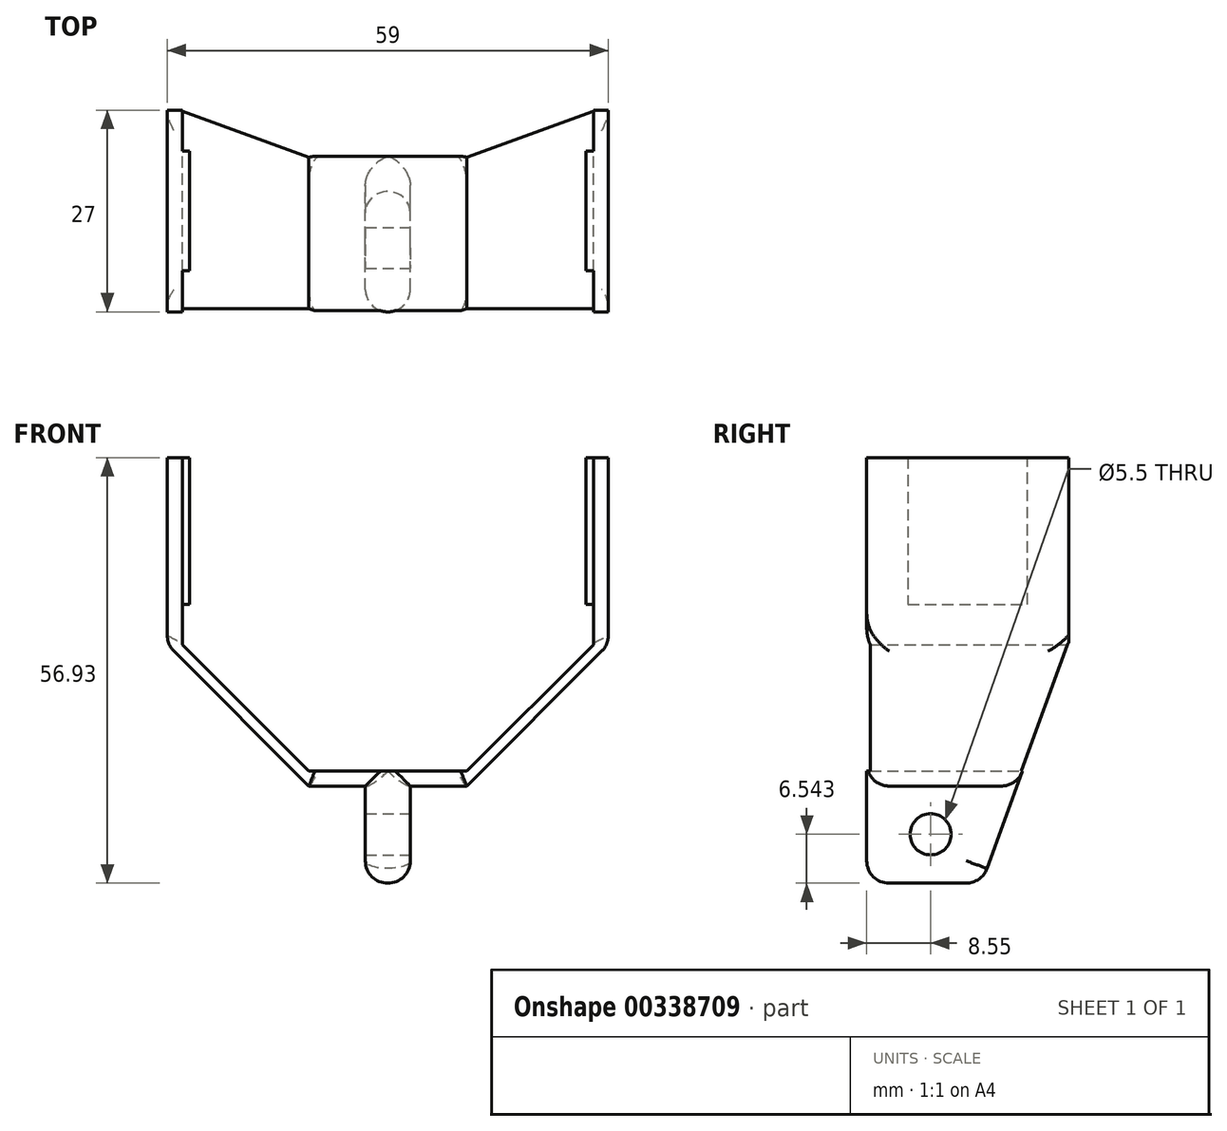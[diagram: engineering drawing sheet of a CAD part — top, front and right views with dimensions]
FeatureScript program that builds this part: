
annotation { "Feature Type Name" : "Feature", "Feature Type Description" : "" }
export const myFeature = defineFeature(function(context is Context, id is Id, definition is map)
    precondition{}
    {
        {
            var Q0;
            Q0=qCreatedBy(makeId("Front.planeOp"),FACE);
            var sketch = newSketch(context, id + "F0", { "sketchPlane" : qUnion([Q0])});
            skLineSegment(sketch, "E0", {"start": v(-27.5, 0) * mm, "end": v(-27.5, 25) * mm});
            skLineSegment(sketch, "E1", {"start": v(-27.5, 25) * mm, "end": v(-29.5, 25) * mm});
            skLineSegment(sketch, "E2", {"start": v(-29.5, 25) * mm, "end": v(-29.5, 0) * mm});
            skLineSegment(sketch, "E3", {"start": v(-29.5, 0) * mm, "end": v(-10.57, -18.93) * mm});
            skLineSegment(sketch, "E4", {"start": v(-27.5, 0) * mm, "end": v(-10.57, -16.93) * mm});
            skLineSegment(sketch, "E5", {"start": v(0, -16.93) * mm, "end": v(-10.57, -16.93) * mm});
            skLineSegment(sketch, "E6", {"start": v(0, -18.93) * mm, "end": v(-10.57, -18.93) * mm});
            skPoint(sketch, "E7.orphan", {"position": v(0, -27.5) * mm});
            skPoint(sketch, "E8.orphan", {"position": v(0, -29.5) * mm});
            skLineSegment(sketch, "E9", {"start": v(-27.5, 0) * mm, "end": v(-27.5, 3.34) * mm});
            skLineSegment(sketch, "E10", {"start": v(-3, -18.93) * mm, "end": v(-3, -31.93) * mm});
            skLineSegment(sketch, "E11", {"start": v(-3, -31.93) * mm, "end": v(0, -31.93) * mm});
            skLineSegment(sketch, "E12", {"start": v(0, -31.93) * mm, "end": v(0, -16.93) * mm});
            skSolve(sketch);
        }
        {
            var Q0;
            {var subQ3=sQuery(id+"F0.wireOp",EDGE,"E10");Q0=makeQuery(id+"F0.imprint","IMPRINT",FACE,{"disambiguationData":[TD([[makeQuery(id+"F0.imprint","IMPRINT",EDGE,{"derivedFrom":subQ3}),1.0]])]});}
            var Q1;
            {var subQ2=sQuery(id+"F0.wireOp",EDGE,"27ad3184-4ef8-43b1-b54a-c4742ede5e2c0.MirrorCS");Q1=makeQuery(id+"F0.imprint","IMPRINT",FACE,{"disambiguationData":[TD([[makeQuery(id+"F0.imprint","IMPRINT",EDGE,{"derivedFrom":subQ2}),-1.0]])]});}
            var Q2;
            {var subQ0=sQuery(id+"F0.wireOp",EDGE,"27ad3184-4ef8-43b1-b54a-c4742ede5e2c1.MirrorCS");Q2=makeQuery(id+"F0.imprint","IMPRINT",FACE,{"disambiguationData":[TD([[makeQuery(id+"F0.imprint","IMPRINT",EDGE,{"derivedFrom":subQ0}),-1.0]])]});}
            var Q3;
            Q3=makeQuery(id+"F0.imprint","IMPRINT",FACE,{"disambiguationData":[TD([[makeQuery(id+"F0.imprint","IMPRINT",EDGE,{"derivedFrom":sQuery(id+"F0.wireOp",EDGE,"E0")}),1.0]])]});
            extrude(context, id + "F1", {"entities" : qUnion([Q0, Q1, Q2, Q3]), "endBound" : BoundingType.SYMMETRIC, "depth" : 27 * mm});
        }
        {
            var Q0;
            Q0=makeQuery(id+"F1.opExtrude","SWEPT_FACE",FACE,{"disambiguationData":[OSD([sQuery(id+"F0.wireOp",EDGE,"E0"),sQuery(id+"F0.wireOp",EDGE,"E9")])]});
            var sketch = newSketch(context, id + "F2", { "sketchPlane" : qUnion([Q0])});
            skLineSegment(sketch, "E13", {"start": v(-8, 25) * mm, "end": v(-8, 5.4) * mm});
            skLineSegment(sketch, "E14", {"start": v(-8, 5.4) * mm, "end": v(8, 5.4) * mm});
            skLineSegment(sketch, "E15", {"start": v(8, 5.4) * mm, "end": v(8, 25) * mm});
            skLineSegment(sketch, "E16", {"start": v(8, 25) * mm, "end": v(-8, 25) * mm});
            skSolve(sketch);
        }
        {
            var Q0;
            Q0=makeQuery(id+"F2.imprint","IMPRINT",FACE,{"disambiguationData":[TD([[makeQuery(id+"F2.imprint","IMPRINT",EDGE,{"derivedFrom":sQuery(id+"F2.wireOp",EDGE,"E13")}),1.0]])]});
            extrude(context, id + "F3", {"entities" : qUnion([Q0]), "operationType" : NewBodyOperationType.ADD, "depth" : 1 * mm});
        }
        {
            var Q0;
            Q0=makeQuery(id+"F1.opExtrude","SWEPT_BODY",BODY,{"disambiguationData":[OSD([sQuery(id+"F0.wireOp",EDGE,"E0"),sQuery(id+"F0.wireOp",EDGE,"E1"),sQuery(id+"F0.wireOp",EDGE,"E2"),sQuery(id+"F0.wireOp",EDGE,"E3"),sQuery(id+"F0.wireOp",EDGE,"E4"),sQuery(id+"F0.wireOp",EDGE,"E5"),sQuery(id+"F0.wireOp",EDGE,"E6"),sQuery(id+"F0.wireOp",EDGE,"E9"),sQuery(id+"F0.wireOp",EDGE,"E10"),sQuery(id+"F0.wireOp",EDGE,"E11"),sQuery(id+"F0.wireOp",EDGE,"E12")])]});
            var Q1;
            Q1=qCreatedBy(makeId("Right.planeOp"),FACE);
            mirror(context, id + "F4", {"operationType" : NewBodyOperationType.ADD, "entities" : qUnion([Q0]), "mirrorPlane" : qUnion([Q1])});
        }
        {
            var Q0;
            Q0=makeQuery(id+"F1.opExtrude","SWEPT_FACE",FACE,{"disambiguationData":[OSD([sQuery(id+"F0.wireOp",EDGE,"E2")])]});
            var sketch = newSketch(context, id + "F5", { "sketchPlane" : qUnion([Q0])});
            skLineSegment(sketch, "E17.MirrorCS", {"start": v(-21.23, 0) * mm, "end": v(-13.5, 0) * mm});
            skLineSegment(sketch, "E18.MirrorCS", {"start": v(-13.5, 0) * mm, "end": v(0.18, -37.59) * mm});
            skLineSegment(sketch, "E19.MirrorCS", {"start": v(-6.55, -39.4) * mm, "end": v(-25.06, -39.4) * mm});
            skLineSegment(sketch, "E20.MirrorCS", {"start": v(-25.06, -39.4) * mm, "end": v(-21.23, 0) * mm});
            skLineSegment(sketch, "E21", {"start": v(-6.55, -39.4) * mm, "end": v(0.18, -37.59) * mm});
            skSolve(sketch);
        }
        {
            var Q0;
            Q0 = qSketchRegion(id + "F5", true);
            extrude(context, id + "F6", {"entities" : qUnion([Q0]), "operationType" : NewBodyOperationType.REMOVE, "endBound" : BoundingType.SYMMETRIC, "depth" : 10000 * mm});
        }
        {
            var Q0;
            Q0=makeQuery(id+"F4.opPattern","COPY",FACE,{"derivedFrom":makeQuery(id+"F1.opExtrude","SWEPT_FACE",FACE,{"disambiguationData":[OSD([sQuery(id+"F0.wireOp",EDGE,"E10")])]}),"instanceName":"1"});
            var sketch = newSketch(context, id + "F7", { "sketchPlane" : qUnion([Q0])});
            skCircle(sketch, "E22", {"center": v(-4.95, -25.39) * mm, "radius": 2.75 * mm});
            skSolve(sketch);
        }
        {
            var Q0;
            Q0=makeQuery(id+"F7.imprint","IMPRINT",FACE,{"disambiguationData":[TD([[makeQuery(id+"F7.imprint","IMPRINT",EDGE,{"derivedFrom":sQuery(id+"F7.wireOp",EDGE,"E22")}),1.0]])]});
            extrude(context, id + "F8", {"entities" : qUnion([Q0]), "operationType" : NewBodyOperationType.REMOVE, "endBound" : BoundingType.SYMMETRIC, "oppositeDirection" : true, "depth" : 100 * mm});
        }
        {
            var Q0;
            {var subQ0=makeQuery(id+"F1.opExtrude","SWEPT_FACE",FACE,{"disambiguationData":[OSD([sQuery(id+"F0.wireOp",EDGE,"E11")])]});Q0=makeQuery(id+"F4.boolean.opBoolean","MERGE",FACE,{"derivedFrom":[subQ0,makeQuery(id+"F4.opPattern","COPY",FACE,{"derivedFrom":subQ0,"instanceName":"1"})]});}
            fillet(context, id + "F9", {"entities" : qUnion([Q0]), "radius" : 3 * mm, "tangentPropagation" : true, "allowEdgeOverflow" : false});
        }
        {
            var Q0;
            Q0=makeQuery(id+"F4.opPattern","COPY",EDGE,{"derivedFrom":makeQuery(id+"F1.opExtrude","CAP_EDGE",EDGE,{"disambiguationData":[OSD([sQuery(id+"F0.wireOp",EDGE,"E10")])],"isStart":false}),"instanceName":"1"});
            var Q1;
            Q1=makeQuery(id+"F1.opExtrude","CAP_EDGE",EDGE,{"disambiguationData":[OSD([sQuery(id+"F0.wireOp",EDGE,"E10")])],"isStart":false});
            var Q2;
            Q2=makeQuery(id+"F4.opPattern","COPY",EDGE,{"derivedFrom":makeQuery(id+"F1.opExtrude","CAP_EDGE",EDGE,{"disambiguationData":[OSD([sQuery(id+"F0.wireOp",EDGE,"E6")])],"isStart":false}),"instanceName":"1"});
            var Q3;
            Q3=makeQuery(id+"F1.opExtrude","CAP_EDGE",EDGE,{"disambiguationData":[OSD([sQuery(id+"F0.wireOp",EDGE,"E6")])],"isStart":false});
            var Q4;
            Q4=makeQuery(id+"F1.opExtrude","CAP_EDGE",EDGE,{"disambiguationData":[OSD([sQuery(id+"F0.wireOp",EDGE,"E3")])],"isStart":false});
            var Q5;
            Q5=makeQuery(id+"F4.opPattern","COPY",EDGE,{"derivedFrom":makeQuery(id+"F1.opExtrude","CAP_EDGE",EDGE,{"disambiguationData":[OSD([sQuery(id+"F0.wireOp",EDGE,"E3")])],"isStart":false}),"instanceName":"1"});
            var Q6;
            Q6=makeQuery(id+"F6.boolean.opBoolean","INTERSECT",EDGE,{"derivedFrom":[makeQuery(id+"F4.opPattern","COPY",FACE,{"derivedFrom":makeQuery(id+"F1.opExtrude","SWEPT_FACE",FACE,{"disambiguationData":[OSD([sQuery(id+"F0.wireOp",EDGE,"E3")])]}),"instanceName":"1"}),makeQuery(id+"F6.opExtrude","SWEPT_FACE",FACE,{"disambiguationData":[OSD([sQuery(id+"F5.wireOp",EDGE,"E18.MirrorCS")])]})]});
            var Q7;
            Q7=makeQuery(id+"F6.boolean.opBoolean","INTERSECT",EDGE,{"derivedFrom":[makeQuery(id+"F4.opPattern","COPY",FACE,{"derivedFrom":makeQuery(id+"F1.opExtrude","SWEPT_FACE",FACE,{"disambiguationData":[OSD([sQuery(id+"F0.wireOp",EDGE,"E6")])]}),"instanceName":"1"}),makeQuery(id+"F6.opExtrude","SWEPT_FACE",FACE,{"disambiguationData":[OSD([sQuery(id+"F5.wireOp",EDGE,"E18.MirrorCS")])]})]});
            var Q8;
            Q8=makeQuery(id+"F6.boolean.opBoolean","INTERSECT",EDGE,{"derivedFrom":[makeQuery(id+"F4.opPattern","COPY",FACE,{"derivedFrom":makeQuery(id+"F1.opExtrude","SWEPT_FACE",FACE,{"disambiguationData":[OSD([sQuery(id+"F0.wireOp",EDGE,"E10")])]}),"instanceName":"1"}),makeQuery(id+"F6.opExtrude","SWEPT_FACE",FACE,{"disambiguationData":[OSD([sQuery(id+"F5.wireOp",EDGE,"E18.MirrorCS")])]})]});
            var Q9;
            Q9=makeQuery(id+"F6.boolean.opBoolean","INTERSECT",EDGE,{"derivedFrom":[makeQuery(id+"F1.opExtrude","SWEPT_FACE",FACE,{"disambiguationData":[OSD([sQuery(id+"F0.wireOp",EDGE,"E10")])]}),makeQuery(id+"F6.opExtrude","SWEPT_FACE",FACE,{"disambiguationData":[OSD([sQuery(id+"F5.wireOp",EDGE,"E18.MirrorCS")])]})]});
            var Q10;
            Q10=makeQuery(id+"F6.boolean.opBoolean","INTERSECT",EDGE,{"derivedFrom":[makeQuery(id+"F1.opExtrude","SWEPT_FACE",FACE,{"disambiguationData":[OSD([sQuery(id+"F0.wireOp",EDGE,"E6")])]}),makeQuery(id+"F6.opExtrude","SWEPT_FACE",FACE,{"disambiguationData":[OSD([sQuery(id+"F5.wireOp",EDGE,"E18.MirrorCS")])]})]});
            var Q11;
            Q11=makeQuery(id+"F6.boolean.opBoolean","INTERSECT",EDGE,{"derivedFrom":[makeQuery(id+"F1.opExtrude","SWEPT_FACE",FACE,{"disambiguationData":[OSD([sQuery(id+"F0.wireOp",EDGE,"E3")])]}),makeQuery(id+"F6.opExtrude","SWEPT_FACE",FACE,{"disambiguationData":[OSD([sQuery(id+"F5.wireOp",EDGE,"E18.MirrorCS")])]})]});
            var Q12;
            Q12=makeQuery(id+"F4.opPattern","COPY",EDGE,{"derivedFrom":makeQuery(id+"F1.opExtrude","SWEPT_EDGE",EDGE,{"disambiguationData":[OSD([sQuery(id+"F0.wireOp",EDGE,"E2"),sQuery(id+"F0.wireOp",EDGE,"E3")])]}),"instanceName":"1"});
            var Q13;
            Q13=makeQuery(id+"F1.opExtrude","SWEPT_EDGE",EDGE,{"disambiguationData":[OSD([sQuery(id+"F0.wireOp",EDGE,"E2"),sQuery(id+"F0.wireOp",EDGE,"E3")])]});
            fillet(context, id + "F10", {"entities" : qUnion([Q0, Q1, Q2, Q3, Q4, Q5, Q6, Q7, Q8, Q9, Q10, Q11, Q12, Q13]), "radius" : 3 * mm, "tangentPropagation" : true, "allowEdgeOverflow" : false});
        }
    });
